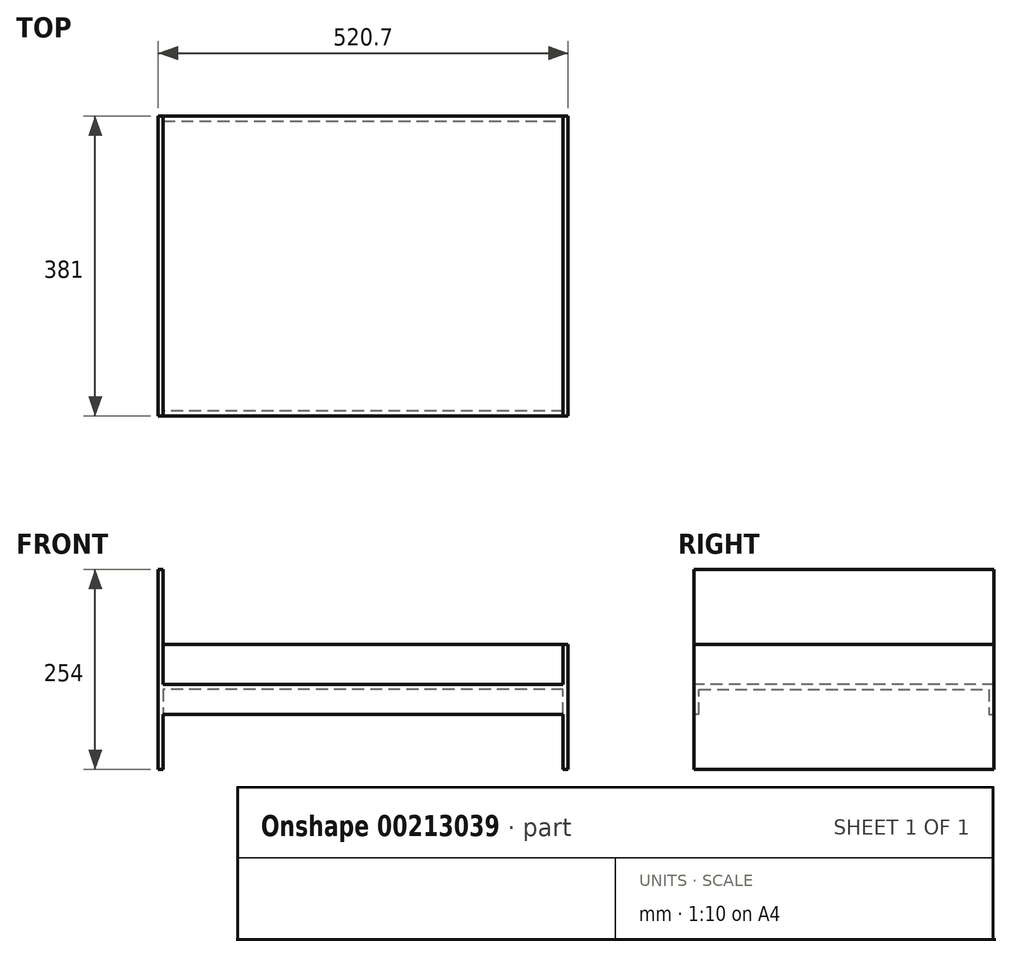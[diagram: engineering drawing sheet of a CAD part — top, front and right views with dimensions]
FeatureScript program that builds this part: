
annotation { "Feature Type Name" : "Feature", "Feature Type Description" : "" }
export const myFeature = defineFeature(function(context is Context, id is Id, definition is map)
    precondition{}
    {
        {
            var Q0;
            Q0=qCreatedBy(makeId("Right.planeOp"),FACE);
            cPlane(context, id + "F0", {"entities" : qUnion([Q0]), "cplaneType" : CPlaneType.OFFSET, "offset" : 508 * mm, "width" : 152.4 * mm, "height" : 152.4 * mm});
        }
        {
            var Q0;
            Q0=qCreatedBy(id+"F0.planeOp",FACE);
            var sketch = newSketch(context, id + "F1", { "sketchPlane" : qUnion([Q0])});
            skLineSegment(sketch, "E0.bottom", {"start": v(-190.5, 0) * mm, "end": v(0, 0) * mm});
            skLineSegment(sketch, "E0.top", {"start": v(-190.5, 158.75) * mm, "end": v(0, 158.75) * mm});
            skLineSegment(sketch, "E0.left", {"start": v(-190.5, 0) * mm, "end": v(-190.5, 158.75) * mm});
            skLineSegment(sketch, "E0.right", {"start": v(0, 0) * mm, "end": v(0, 158.75) * mm});
            skSolve(sketch);
        }
        {
            var Q0;
            Q0 = qSketchRegion(id + "F1", true);
            extrude(context, id + "F2", {"entities" : qUnion([Q0]), "depth" : 6.35 * mm});
        }
        {
            var Q0;
            Q0=qCreatedBy(makeId("Right.planeOp"),FACE);
            var sketch = newSketch(context, id + "F3", { "sketchPlane" : qUnion([Q0])});
            skLineSegment(sketch, "E1.bottom", {"start": v(0, 0) * mm, "end": v(-190.5, 0) * mm});
            skLineSegment(sketch, "E1.top", {"start": v(0, 254) * mm, "end": v(-190.5, 254) * mm});
            skLineSegment(sketch, "E1.left", {"start": v(0, 0) * mm, "end": v(0, 254) * mm});
            skLineSegment(sketch, "E1.right", {"start": v(-190.5, 0) * mm, "end": v(-190.5, 254) * mm});
            skSolve(sketch);
        }
        {
            var Q0;
            Q0 = qSketchRegion(id + "F3", true);
            extrude(context, id + "F4", {"entities" : qUnion([Q0]), "oppositeDirection" : true, "depth" : 6.35 * mm});
        }
        {
            var Q0;
            Q0=makeQuery(id+"F2.opExtrude","SWEPT_FACE",FACE,{"disambiguationData":[OSD([sQuery(id+"F1.wireOp",EDGE,"E0.left")])]});
            var sketch = newSketch(context, id + "F5", { "sketchPlane" : qUnion([Q0])});
            skLineSegment(sketch, "E2.bottom", {"start": v(508, 107.95) * mm, "end": v(0, 107.95) * mm});
            skLineSegment(sketch, "E2.top", {"start": v(508, 69.85) * mm, "end": v(0, 69.85) * mm});
            skLineSegment(sketch, "E2.left", {"start": v(508, 107.95) * mm, "end": v(508, 69.85) * mm});
            skLineSegment(sketch, "E2.right", {"start": v(0, 107.95) * mm, "end": v(0, 69.85) * mm});
            skSolve(sketch);
        }
        {
            var Q0;
            Q0=makeQuery(id+"F5.imprint","IMPRINT",FACE,{"disambiguationData":[TD([[makeQuery(id+"F5.imprint","IMPRINT",EDGE,{"derivedFrom":sQuery(id+"F5.wireOp",EDGE,"E2.bottom")}),1.0]])]});
            extrude(context, id + "F6", {"entities" : qUnion([Q0]), "operationType" : NewBodyOperationType.ADD, "oppositeDirection" : true, "depth" : 6.35 * mm});
        }
        {
            var Q0;
            Q0=makeQuery(id+"F2.opExtrude","SWEPT_BODY",BODY,{"disambiguationData":[OSD([sQuery(id+"F1.wireOp",EDGE,"E0.bottom"),sQuery(id+"F1.wireOp",EDGE,"E0.top"),sQuery(id+"F1.wireOp",EDGE,"E0.left"),sQuery(id+"F1.wireOp",EDGE,"E0.right")])]});
            var Q1;
            Q1=qCreatedBy(makeId("Front.planeOp"),FACE);
            mirror(context, id + "F7", {"operationType" : NewBodyOperationType.ADD, "entities" : qUnion([Q0]), "mirrorPlane" : qUnion([Q1])});
        }
        {
            var Q0;
            Q0=makeQuery(id+"F6.opExtrude","SWEPT_FACE",FACE,{"disambiguationData":[OSD([sQuery(id+"F5.wireOp",EDGE,"E2.bottom")])]});
            var sketch = newSketch(context, id + "F8", { "sketchPlane" : qUnion([Q0])});
            skLineSegment(sketch, "E3.bottom", {"start": v(0, -184.15) * mm, "end": v(508, -184.15) * mm});
            skLineSegment(sketch, "E3.top", {"start": v(0, 184.15) * mm, "end": v(508, 184.15) * mm});
            skLineSegment(sketch, "E3.left", {"start": v(0, -184.15) * mm, "end": v(0, 184.15) * mm});
            skLineSegment(sketch, "E3.right", {"start": v(508, -184.15) * mm, "end": v(508, 184.15) * mm});
            skSolve(sketch);
        }
        {
            var Q0;
            Q0=makeQuery(id+"F8.imprint","IMPRINT",FACE,{"disambiguationData":[TD([[makeQuery(id+"F8.imprint","IMPRINT",EDGE,{"derivedFrom":sQuery(id+"F8.wireOp",EDGE,"E3.bottom")}),-1.0]])]});
            extrude(context, id + "F9", {"entities" : qUnion([Q0]), "operationType" : NewBodyOperationType.ADD, "oppositeDirection" : true, "depth" : 6.35 * mm});
        }
        {
            var Q0;
            {var subQ0=makeQuery(id+"F6.opExtrude","SWEPT_FACE",FACE,{"disambiguationData":[OSD([sQuery(id+"F5.wireOp",EDGE,"E2.bottom")])]});Q0=makeQuery(id+"F9.boolean.opBoolean","MERGE",FACE,{"derivedFrom":[subQ0,makeQuery(id+"F7.opPattern","COPY",FACE,{"derivedFrom":subQ0,"instanceName":"1"}),makeQuery(id+"F9.opExtrude","CAP_FACE",FACE,{"disambiguationData":[OSD([sQuery(id+"F8.wireOp",EDGE,"E3.bottom"),sQuery(id+"F8.wireOp",EDGE,"E3.top"),sQuery(id+"F8.wireOp",EDGE,"E3.left"),sQuery(id+"F8.wireOp",EDGE,"E3.right")])],"isStart":true})]});}
            var sketch = newSketch(context, id + "F10", { "sketchPlane" : qUnion([Q0])});
            skLineSegment(sketch, "E4.bottom", {"start": v(0, -190.5) * mm, "end": v(508, -190.5) * mm});
            skLineSegment(sketch, "E4.top", {"start": v(0, 190.5) * mm, "end": v(508, 190.5) * mm});
            skLineSegment(sketch, "E4.left", {"start": v(0, -190.5) * mm, "end": v(0, 190.5) * mm});
            skLineSegment(sketch, "E4.right", {"start": v(508, -190.5) * mm, "end": v(508, 190.5) * mm});
            skSolve(sketch);
        }
        {
            var Q0;
            Q0=makeQuery(id+"F10.imprint","IMPRINT",FACE,{"disambiguationData":[TD([[makeQuery(id+"F10.imprint","IMPRINT",EDGE,{"derivedFrom":sQuery(id+"F10.wireOp",EDGE,"E4.bottom")}),-1.0]])]});
            extrude(context, id + "F11", {"entities" : qUnion([Q0]), "depth" : 50.8 * mm});
        }
    });
